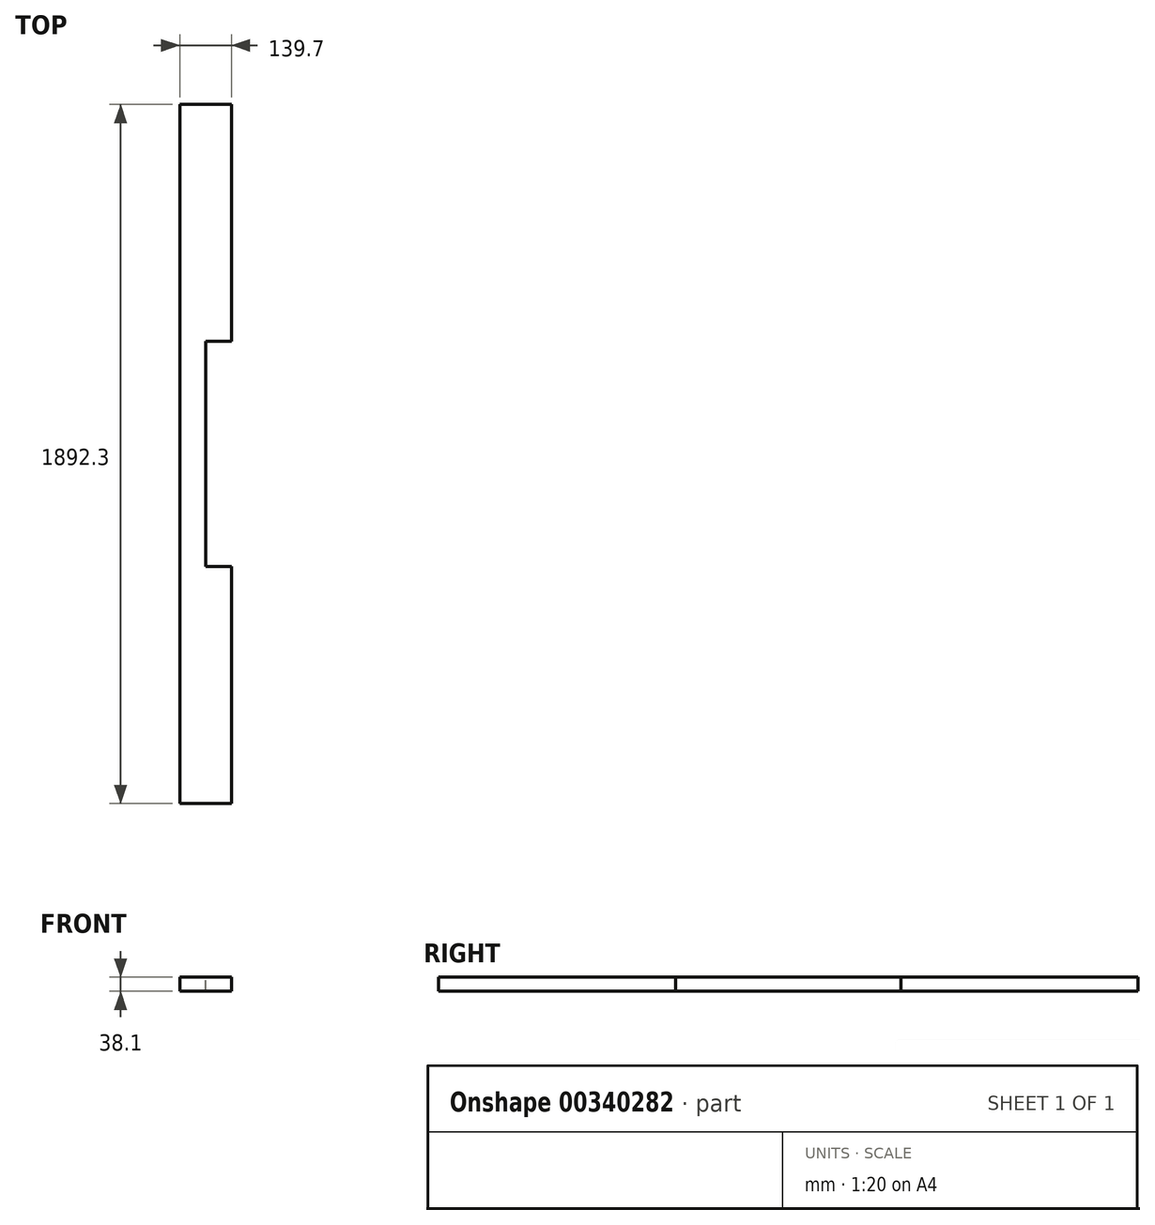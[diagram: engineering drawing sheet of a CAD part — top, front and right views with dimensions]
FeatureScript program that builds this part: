
annotation { "Feature Type Name" : "Feature", "Feature Type Description" : "" }
export const myFeature = defineFeature(function(context is Context, id is Id, definition is map)
    precondition{}
    {
        {
            var Q0;
            Q0=qCreatedBy(makeId("Front.planeOp"),FACE);
            var sketch = newSketch(context, id + "F0", { "sketchPlane" : qUnion([Q0])});
            skLineSegment(sketch, "E0.bottom", {"start": v(69.85, -19.05) * mm, "end": v(-69.85, -19.05) * mm});
            skLineSegment(sketch, "E0.top", {"start": v(69.85, 19.05) * mm, "end": v(-69.85, 19.05) * mm});
            skLineSegment(sketch, "E0.left", {"start": v(69.85, -19.05) * mm, "end": v(69.85, 19.05) * mm});
            skLineSegment(sketch, "E0.right", {"start": v(-69.85, -19.05) * mm, "end": v(-69.85, 19.05) * mm});
            skPoint(sketch, "E0.middle", {"position": v(0, 0) * mm});
            skSolve(sketch);
        }
        {
            var Q0;
            Q0=qSketchRegion(id+"F0",true);
            extrude(context, id + "F1", {"entities" : qUnion([Q0]), "endBound" : BoundingType.SYMMETRIC, "depth" : 1892.3 * mm});
        }
        {
            var Q0;
            Q0=makeQuery(id+"F1.opExtrude","SWEPT_FACE",FACE,{"disambiguationData":[OSD([sQuery(id+"F0.wireOp",EDGE,"E0.top")])]});
            var sketch = newSketch(context, id + "F2", { "sketchPlane" : qUnion([Q0])});
            skLineSegment(sketch, "E1.bottom", {"start": v(0, -304.8) * mm, "end": v(139.7, -304.8) * mm});
            skLineSegment(sketch, "E1.top", {"start": v(0, 304.8) * mm, "end": v(139.7, 304.8) * mm});
            skLineSegment(sketch, "E1.left", {"start": v(0, -304.8) * mm, "end": v(0, 304.8) * mm});
            skLineSegment(sketch, "E1.right", {"start": v(139.7, -304.8) * mm, "end": v(139.7, 304.8) * mm});
            skPoint(sketch, "E1.middle", {"position": v(69.85, 0) * mm});
            skSolve(sketch);
        }
        {
            var Q0;
            Q0 = qSketchRegion(id + "F2", true);
            extrude(context, id + "F3", {"entities" : qUnion([Q0]), "operationType" : NewBodyOperationType.REMOVE, "endBound" : BoundingType.THROUGH_ALL, "oppositeDirection" : true, "depth" : 25.4 * mm});
        }
    });
